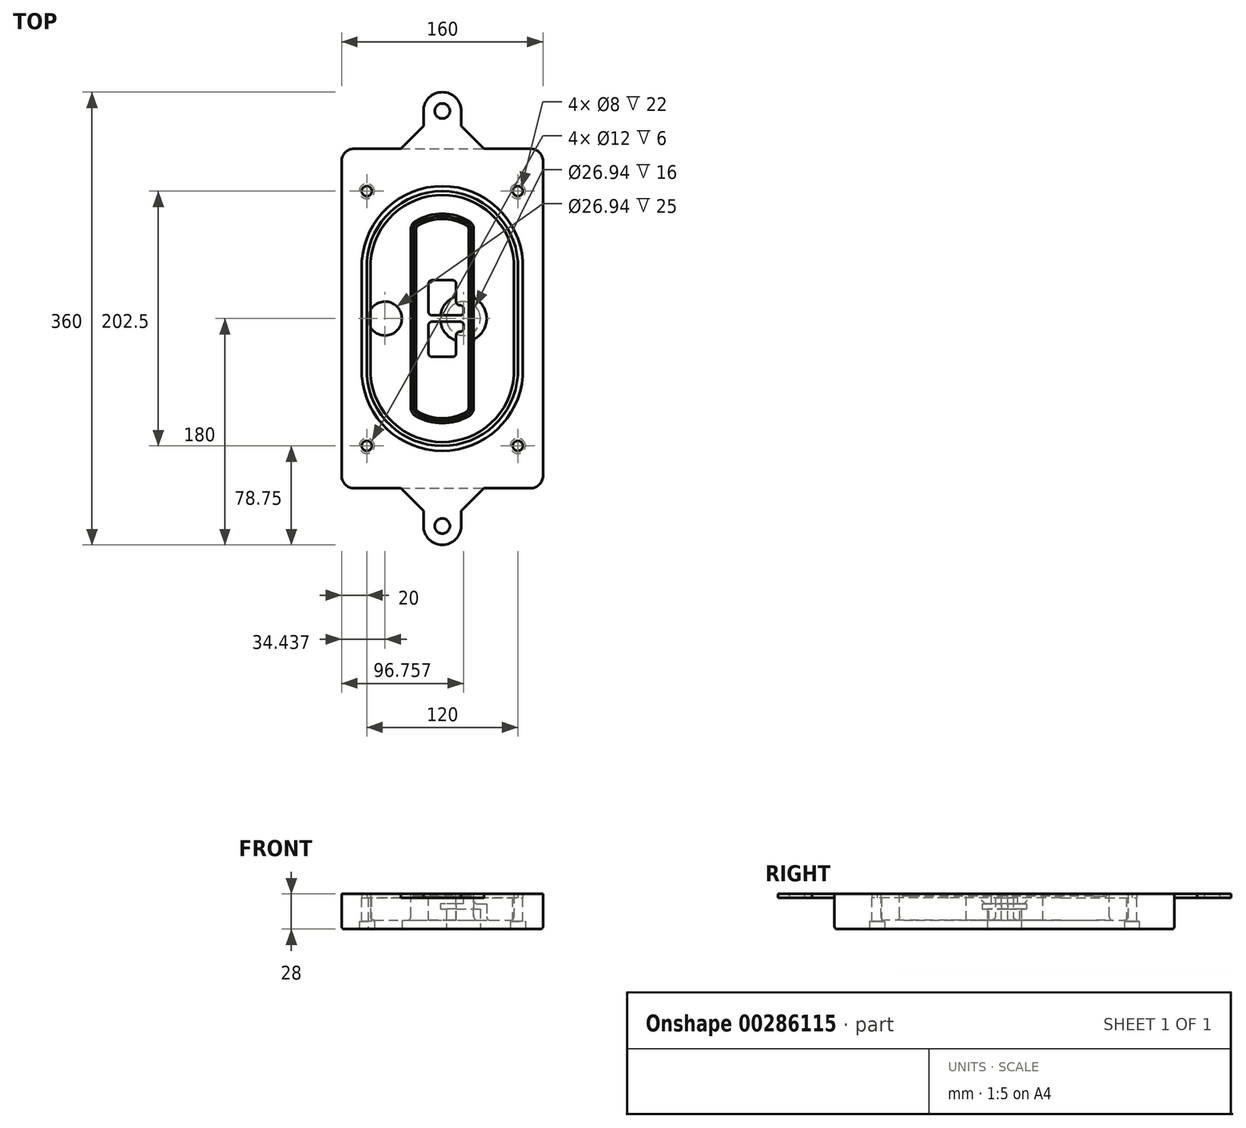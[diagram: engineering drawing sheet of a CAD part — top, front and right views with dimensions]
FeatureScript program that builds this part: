
annotation { "Feature Type Name" : "Feature", "Feature Type Description" : "" }
export const myFeature = defineFeature(function(context is Context, id is Id, definition is map)
    precondition{}
    {
        {
            var Q0;
            Q0=qCreatedBy(makeId("Top.planeOp"),FACE);
            var sketch = newSketch(context, id + "F0", { "sketchPlane" : qUnion([Q0])});
            skPoint(sketch, "E0.rect.middle", {"position": v(0, 0) * mm});
            skLineSegment(sketch, "E1.bottom", {"start": v(-70, -135) * mm, "end": v(70, -135) * mm});
            skLineSegment(sketch, "E1.top", {"start": v(-70, 135) * mm, "end": v(70, 135) * mm});
            skLineSegment(sketch, "E1.left", {"start": v(-80, -125) * mm, "end": v(-80, 125) * mm});
            skLineSegment(sketch, "E1.right", {"start": v(80, -125) * mm, "end": v(80, 125) * mm});
            skLineSegment(sketch, "E2", {"start": v(-80, 135) * mm, "end": v(80, -135) * mm, "construction": true});
            skLineSegment(sketch, "E3", {"start": v(80, 135) * mm, "end": v(-80, -135) * mm, "construction": true});
            skCircle(sketch, "E4", {"center": v(-60, 101.25) * mm, "radius": 4 * mm});
            skCircle(sketch, "E5", {"center": v(60, 101.25) * mm, "radius": 4 * mm});
            skCircle(sketch, "E6", {"center": v(60, -101.25) * mm, "radius": 4 * mm});
            skCircle(sketch, "E7", {"center": v(-60, -101.25) * mm, "radius": 4 * mm});
            skLineSegment(sketch, "E8", {"start": v(-60, 101.25) * mm, "end": v(60, 101.25) * mm, "construction": true});
            skLineSegment(sketch, "E9", {"start": v(60, 101.25) * mm, "end": v(60, -101.25) * mm, "construction": true});
            skLineSegment(sketch, "E10", {"start": v(60, -101.25) * mm, "end": v(-60, -101.25) * mm, "construction": true});
            skLineSegment(sketch, "E11", {"start": v(-60, -101.25) * mm, "end": v(-60, 101.25) * mm, "construction": true});
            skLineSegment(sketch, "E12", {"start": v(-60, 44.66) * mm, "end": v(-60, -44.66) * mm});
            skLineSegment(sketch, "E13", {"start": v(60, 44.66) * mm, "end": v(60, -44.66) * mm});
            skArc(sketch, "E14", {"start": v(59.98, 45.37) * mm, "mid": v(0, 101.25) * mm, "end": v(-59.98, 45.37) * mm});
            skArc(sketch, "E15", {"start": v(-59.98, -45.37) * mm, "mid": v(0, -101.25) * mm, "end": v(59.98, -45.37) * mm});
            skLineSegment(sketch, "E16", {"start": v(-60, 0) * mm, "end": v(60, 0) * mm, "construction": true});
            skPoint(sketch, "E17.visualSharp", {"position": v(-60, -45) * mm});
            skArc(sketch, "E17.filletArc", {"start": v(-60, -44.66) * mm, "mid": v(-60, -45.02) * mm, "end": v(-59.98, -45.37) * mm});
            skPoint(sketch, "E18.visualSharp", {"position": v(-60, 45) * mm});
            skArc(sketch, "E18.filletArc", {"start": v(-59.98, 45.37) * mm, "mid": v(-60, 45.02) * mm, "end": v(-60, 44.66) * mm});
            skPoint(sketch, "E19.visualSharp", {"position": v(60, 45) * mm});
            skArc(sketch, "E19.filletArc", {"start": v(60, 44.66) * mm, "mid": v(60, 45.02) * mm, "end": v(59.98, 45.37) * mm});
            skPoint(sketch, "E20.visualSharp", {"position": v(60, -45) * mm});
            skArc(sketch, "E20.filletArc", {"start": v(59.98, -45.37) * mm, "mid": v(60, -45.02) * mm, "end": v(60, -44.66) * mm});
            skPoint(sketch, "E21.visualSharp", {"position": v(-80, 135) * mm});
            skArc(sketch, "E21.filletArc", {"start": v(-70, 135) * mm, "mid": v(-77.07, 132.07) * mm, "end": v(-80, 125) * mm});
            skPoint(sketch, "E22.visualSharp", {"position": v(80, 135) * mm});
            skArc(sketch, "E22.filletArc", {"start": v(80, 125) * mm, "mid": v(77.07, 132.07) * mm, "end": v(70, 135) * mm});
            skPoint(sketch, "E23.visualSharp", {"position": v(80, -135) * mm});
            skArc(sketch, "E23.filletArc", {"start": v(70, -135) * mm, "mid": v(77.07, -132.07) * mm, "end": v(80, -125) * mm});
            skPoint(sketch, "E24.visualSharp", {"position": v(-80, -135) * mm});
            skArc(sketch, "E24.filletArc", {"start": v(-80, -125) * mm, "mid": v(-77.07, -132.07) * mm, "end": v(-70, -135) * mm});
            skArc(sketch, "E25.0", {"start": v(57, 44.66) * mm, "mid": v(57, 44.9) * mm, "end": v(56.98, 45.16) * mm});
            skLineSegment(sketch, "E25.1", {"start": v(57, 44.66) * mm, "end": v(57, -44.66) * mm});
            skArc(sketch, "E25.2", {"start": v(56.98, -45.16) * mm, "mid": v(57, -44.9) * mm, "end": v(57, -44.66) * mm});
            skArc(sketch, "E25.3", {"start": v(-56.98, -45.16) * mm, "mid": v(0, -98.25) * mm, "end": v(56.98, -45.16) * mm});
            skArc(sketch, "E25.4", {"start": v(-57, -44.66) * mm, "mid": v(-57, -44.9) * mm, "end": v(-56.98, -45.16) * mm});
            skArc(sketch, "E25.5", {"start": v(56.98, 45.16) * mm, "mid": v(0, 98.25) * mm, "end": v(-56.98, 45.16) * mm});
            skLineSegment(sketch, "E25.6", {"start": v(-57, 44.66) * mm, "end": v(-57, -44.66) * mm});
            skArc(sketch, "E25.7", {"start": v(-56.98, 45.16) * mm, "mid": v(-57, 44.9) * mm, "end": v(-57, 44.66) * mm});
            skArc(sketch, "E26.0", {"start": v(-63.97, 45.65) * mm, "mid": v(-64, 45.16) * mm, "end": v(-64, 44.66) * mm});
            skArc(sketch, "E26.1", {"start": v(63.97, 45.65) * mm, "mid": v(0, 105.25) * mm, "end": v(-63.97, 45.65) * mm});
            skArc(sketch, "E26.2", {"start": v(64, 44.66) * mm, "mid": v(64, 45.16) * mm, "end": v(63.97, 45.65) * mm});
            skLineSegment(sketch, "E26.3", {"start": v(64, 44.66) * mm, "end": v(64, -44.66) * mm});
            skArc(sketch, "E26.4", {"start": v(63.97, -45.65) * mm, "mid": v(64, -45.16) * mm, "end": v(64, -44.66) * mm});
            skLineSegment(sketch, "E26.5", {"start": v(-64, 44.66) * mm, "end": v(-64, -44.66) * mm});
            skArc(sketch, "E26.6", {"start": v(-63.97, -45.65) * mm, "mid": v(0, -105.25) * mm, "end": v(63.97, -45.65) * mm});
            skArc(sketch, "E26.7", {"start": v(-64, -44.66) * mm, "mid": v(-64, -45.16) * mm, "end": v(-63.97, -45.65) * mm});
            skSolve(sketch);
        }
        {
            var Q0;
            Q0=makeQuery(id+"F0.imprint","IMPRINT",FACE,{"disambiguationData":[TD([[makeQuery(id+"F0.imprint","IMPRINT",EDGE,{"derivedFrom":sQuery(id+"F0.wireOp",EDGE,"E1.bottom")}),1.0]])]});
            var Q1;
            Q1=makeQuery(id+"F0.imprint","IMPRINT",FACE,{"disambiguationData":[TD([[makeQuery(id+"F0.imprint","IMPRINT",EDGE,{"derivedFrom":sQuery(id+"F0.wireOp",EDGE,"E12")}),1.0]])]});
            var Q2;
            Q2=makeQuery(id+"F0.imprint","IMPRINT",FACE,{"disambiguationData":[TD([[makeQuery(id+"F0.imprint","IMPRINT",EDGE,{"derivedFrom":sQuery(id+"F0.wireOp",EDGE,"E25.0")}),1.0]])]});
            var Q3;
            Q3=makeQuery(id+"F0.imprint","IMPRINT",FACE,{"disambiguationData":[TD([[makeQuery(id+"F0.imprint","IMPRINT",EDGE,{"derivedFrom":sQuery(id+"F0.wireOp",EDGE,"E12")}),-1.0]])]});
            extrude(context, id + "F1", {"entities" : qUnion([Q0, Q1, Q2, Q3]), "oppositeDirection" : true, "depth" : 25 * mm});
        }
        {
            var Q0;
            Q0=makeQuery(id+"F0.imprint","IMPRINT",FACE,{"disambiguationData":[TD([[makeQuery(id+"F0.imprint","IMPRINT",EDGE,{"derivedFrom":sQuery(id+"F0.wireOp",EDGE,"E12")}),1.0]])]});
            extrude(context, id + "F2", {"entities" : qUnion([Q0]), "operationType" : NewBodyOperationType.ADD, "depth" : 3 * mm});
        }
        {
            var Q0;
            Q0=makeQuery(id+"F0.imprint","IMPRINT",FACE,{"disambiguationData":[TD([[makeQuery(id+"F0.imprint","IMPRINT",EDGE,{"derivedFrom":sQuery(id+"F0.wireOp",EDGE,"E25.0")}),1.0]])]});
            extrude(context, id + "F3", {"entities" : qUnion([Q0]), "operationType" : NewBodyOperationType.REMOVE, "oppositeDirection" : true, "depth" : 18 * mm});
        }
        {
            var Q0;
            Q0=makeQuery(id+"F2.opExtrude","CAP_FACE",FACE,{"disambiguationData":[OSD([sQuery(id+"F0.wireOp",EDGE,"E12"),sQuery(id+"F0.wireOp",EDGE,"E13"),sQuery(id+"F0.wireOp",EDGE,"E14"),sQuery(id+"F0.wireOp",EDGE,"E15"),sQuery(id+"F0.wireOp",EDGE,"E17.filletArc"),sQuery(id+"F0.wireOp",EDGE,"E18.filletArc"),sQuery(id+"F0.wireOp",EDGE,"E19.filletArc"),sQuery(id+"F0.wireOp",EDGE,"E20.filletArc"),sQuery(id+"F0.wireOp",EDGE,"E25.0"),sQuery(id+"F0.wireOp",EDGE,"E25.1"),sQuery(id+"F0.wireOp",EDGE,"E25.2"),sQuery(id+"F0.wireOp",EDGE,"E25.3"),sQuery(id+"F0.wireOp",EDGE,"E25.4"),sQuery(id+"F0.wireOp",EDGE,"E25.5"),sQuery(id+"F0.wireOp",EDGE,"E25.6"),sQuery(id+"F0.wireOp",EDGE,"E25.7")])],"isStart":false});
            var sketch = newSketch(context, id + "F4", { "sketchPlane" : qUnion([Q0])});
            skArc(sketch, "E27.0", {"start": v(-20.99, -77.65) * mm, "mid": v(0, -83.25) * mm, "end": v(20.99, -77.65) * mm});
            skArc(sketch, "E28.0", {"start": v(20.99, 77.65) * mm, "mid": v(0, 83.25) * mm, "end": v(-20.99, 77.65) * mm});
            skLineSegment(sketch, "E29", {"start": v(-25, 70.71) * mm, "end": v(-25, -70.71) * mm});
            skLineSegment(sketch, "E30", {"start": v(25, 70.71) * mm, "end": v(25, -70.71) * mm});
            skLineSegment(sketch, "E31", {"start": v(-25, 75.03) * mm, "end": v(25, 75.03) * mm, "construction": true});
            skLineSegment(sketch, "E32", {"start": v(-25, -75.03) * mm, "end": v(25, -75.03) * mm, "construction": true});
            skPoint(sketch, "E33.visualSharp", {"position": v(-25, 75.03) * mm});
            skArc(sketch, "E33.filletArc", {"start": v(-20.99, 77.65) * mm, "mid": v(-23.92, 74.72) * mm, "end": v(-25, 70.71) * mm});
            skPoint(sketch, "E34.visualSharp", {"position": v(25, 75.03) * mm});
            skArc(sketch, "E34.filletArc", {"start": v(25, 70.71) * mm, "mid": v(23.92, 74.72) * mm, "end": v(20.99, 77.65) * mm});
            skPoint(sketch, "E35.visualSharp", {"position": v(25, -75.03) * mm});
            skArc(sketch, "E35.filletArc", {"start": v(20.99, -77.65) * mm, "mid": v(23.92, -74.72) * mm, "end": v(25, -70.71) * mm});
            skPoint(sketch, "E36.visualSharp", {"position": v(-25, -75.03) * mm});
            skArc(sketch, "E36.filletArc", {"start": v(-25, -70.71) * mm, "mid": v(-23.92, -74.72) * mm, "end": v(-20.99, -77.65) * mm});
            skArc(sketch, "E37.0", {"start": v(56.98, 45.16) * mm, "mid": v(0, 98.25) * mm, "end": v(-56.98, 45.16) * mm});
            skArc(sketch, "E37.1", {"start": v(-56.98, 45.16) * mm, "mid": v(-57, 44.9) * mm, "end": v(-57, 44.66) * mm});
            skLineSegment(sketch, "E37.2", {"start": v(-57, 44.66) * mm, "end": v(-57, -44.66) * mm});
            skArc(sketch, "E37.3", {"start": v(-57, -44.66) * mm, "mid": v(-57, -44.9) * mm, "end": v(-56.98, -45.16) * mm});
            skArc(sketch, "E37.4", {"start": v(-56.98, -45.16) * mm, "mid": v(0, -98.25) * mm, "end": v(56.98, -45.16) * mm});
            skArc(sketch, "E37.5", {"start": v(56.98, -45.16) * mm, "mid": v(57, -44.9) * mm, "end": v(57, -44.66) * mm});
            skLineSegment(sketch, "E37.6", {"start": v(57, 44.66) * mm, "end": v(57, -44.66) * mm});
            skArc(sketch, "E37.7", {"start": v(57, 44.66) * mm, "mid": v(57, 44.9) * mm, "end": v(56.98, 45.16) * mm});
            skLineSegment(sketch, "E38.0", {"start": v(23, 70.71) * mm, "end": v(23, -70.71) * mm});
            skArc(sketch, "E38.1", {"start": v(19.99, -75.92) * mm, "mid": v(22.2, -73.72) * mm, "end": v(23, -70.71) * mm});
            skArc(sketch, "E38.2", {"start": v(-19.99, -75.92) * mm, "mid": v(0, -81.25) * mm, "end": v(19.99, -75.92) * mm});
            skArc(sketch, "E38.3", {"start": v(-23, -70.71) * mm, "mid": v(-22.2, -73.72) * mm, "end": v(-19.99, -75.92) * mm});
            skLineSegment(sketch, "E38.4", {"start": v(-23, 70.71) * mm, "end": v(-23, -70.71) * mm});
            skArc(sketch, "E38.5", {"start": v(23, 70.71) * mm, "mid": v(22.2, 73.72) * mm, "end": v(19.99, 75.92) * mm});
            skArc(sketch, "E38.6", {"start": v(-19.99, 75.92) * mm, "mid": v(-22.2, 73.72) * mm, "end": v(-23, 70.71) * mm});
            skArc(sketch, "E38.7", {"start": v(19.99, 75.92) * mm, "mid": v(0, 81.25) * mm, "end": v(-19.99, 75.92) * mm});
            skArc(sketch, "E39.0", {"start": v(21, 70.71) * mm, "mid": v(20.46, 72.72) * mm, "end": v(19, 74.18) * mm});
            skLineSegment(sketch, "E39.1", {"start": v(21, 70.71) * mm, "end": v(21, -70.71) * mm});
            skArc(sketch, "E39.2", {"start": v(19, -74.18) * mm, "mid": v(20.46, -72.72) * mm, "end": v(21, -70.71) * mm});
            skArc(sketch, "E39.3", {"start": v(-19, -74.18) * mm, "mid": v(0, -79.25) * mm, "end": v(19, -74.18) * mm});
            skArc(sketch, "E39.4", {"start": v(-21, -70.71) * mm, "mid": v(-20.46, -72.72) * mm, "end": v(-19, -74.18) * mm});
            skArc(sketch, "E39.5", {"start": v(19, 74.18) * mm, "mid": v(0, 79.25) * mm, "end": v(-19, 74.18) * mm});
            skLineSegment(sketch, "E39.6", {"start": v(-21, 70.71) * mm, "end": v(-21, -70.71) * mm});
            skArc(sketch, "E39.7", {"start": v(-19, 74.18) * mm, "mid": v(-20.46, 72.72) * mm, "end": v(-21, 70.71) * mm});
            skLineSegment(sketch, "E40", {"start": v(-25, 0) * mm, "end": v(25, 0) * mm, "construction": true});
            skLineSegment(sketch, "E41", {"start": v(-11, 5.5) * mm, "end": v(-11, 27.5) * mm});
            skLineSegment(sketch, "E42", {"start": v(-8, 30.5) * mm, "end": v(8, 30.5) * mm});
            skLineSegment(sketch, "E43", {"start": v(11, 27.5) * mm, "end": v(11, 13.5) * mm});
            skLineSegment(sketch, "E44", {"start": v(14, 10.5) * mm, "end": v(14, 10.5) * mm});
            skLineSegment(sketch, "E45", {"start": v(17, 7.5) * mm, "end": v(17, 5.5) * mm});
            skLineSegment(sketch, "E46", {"start": v(14, 2.5) * mm, "end": v(-8, 2.5) * mm});
            skPoint(sketch, "E47.visualSharp", {"position": v(-11, 30.5) * mm});
            skArc(sketch, "E47.filletArc", {"start": v(-8, 30.5) * mm, "mid": v(-10.12, 29.62) * mm, "end": v(-11, 27.5) * mm});
            skPoint(sketch, "E48.visualSharp", {"position": v(11, 30.5) * mm});
            skArc(sketch, "E48.filletArc", {"start": v(11, 27.5) * mm, "mid": v(10.12, 29.62) * mm, "end": v(8, 30.5) * mm});
            skPoint(sketch, "E49.visualSharp", {"position": v(11, 10.5) * mm});
            skArc(sketch, "E49.filletArc", {"start": v(11, 13.5) * mm, "mid": v(11.88, 11.38) * mm, "end": v(14, 10.5) * mm});
            skPoint(sketch, "E50.visualSharp", {"position": v(17, 10.5) * mm});
            skArc(sketch, "E50.filletArc", {"start": v(17, 7.5) * mm, "mid": v(16.12, 9.62) * mm, "end": v(14, 10.5) * mm});
            skPoint(sketch, "E51.visualSharp", {"position": v(17, 2.5) * mm});
            skArc(sketch, "E51.filletArc", {"start": v(14, 2.5) * mm, "mid": v(16.12, 3.38) * mm, "end": v(17, 5.5) * mm});
            skPoint(sketch, "E52.visualSharp", {"position": v(-11, 2.5) * mm});
            skArc(sketch, "E52.filletArc", {"start": v(-11, 5.5) * mm, "mid": v(-10.12, 3.38) * mm, "end": v(-8, 2.5) * mm});
            skLineSegment(sketch, "E53.0.MirrorCS", {"start": v(14, -2.5) * mm, "end": v(-8, -2.5) * mm});
            skArc(sketch, "E54.0.MirrorCS", {"start": v(-11, -5.5) * mm, "mid": v(-10.12, -3.38) * mm, "end": v(-8, -2.5) * mm});
            skLineSegment(sketch, "E55.0.MirrorCS", {"start": v(-11, -5.5) * mm, "end": v(-11, -27.5) * mm});
            skArc(sketch, "E56.0.MirrorCS", {"start": v(-8, -30.5) * mm, "mid": v(-10.12, -29.62) * mm, "end": v(-11, -27.5) * mm});
            skLineSegment(sketch, "E57.0.MirrorCS", {"start": v(-8, -30.5) * mm, "end": v(8, -30.5) * mm});
            skArc(sketch, "E58.0.MirrorCS", {"start": v(11, -27.5) * mm, "mid": v(10.12, -29.62) * mm, "end": v(8, -30.5) * mm});
            skLineSegment(sketch, "E59.0.MirrorCS", {"start": v(11, -27.5) * mm, "end": v(11, -13.5) * mm});
            skArc(sketch, "E60.0.MirrorCS", {"start": v(11, -13.5) * mm, "mid": v(11.88, -11.38) * mm, "end": v(14, -10.5) * mm});
            skArc(sketch, "E61.0.MirrorCS", {"start": v(17, -7.5) * mm, "mid": v(16.12, -9.62) * mm, "end": v(14, -10.5) * mm});
            skLineSegment(sketch, "E62.0.MirrorCS", {"start": v(17, -7.5) * mm, "end": v(17, -5.5) * mm});
            skArc(sketch, "E63.0.MirrorCS", {"start": v(14, -2.5) * mm, "mid": v(16.12, -3.38) * mm, "end": v(17, -5.5) * mm});
            skSolve(sketch);
        }
        {
            var Q0;
            Q0=makeQuery(id+"F4.imprint","IMPRINT",FACE,{"disambiguationData":[TD([[makeQuery(id+"F4.imprint","IMPRINT",EDGE,{"derivedFrom":sQuery(id+"F4.wireOp",EDGE,"E27.0")}),1.0]])]});
            var Q1;
            Q1=makeQuery(id+"F4.imprint","IMPRINT",FACE,{"disambiguationData":[TD([[makeQuery(id+"F4.imprint","IMPRINT",EDGE,{"derivedFrom":sQuery(id+"F4.wireOp",EDGE,"E38.0")}),-1.0]])]});
            var Q2;
            Q2=makeQuery(id+"F4.imprint","IMPRINT",FACE,{"disambiguationData":[TD([[makeQuery(id+"F4.imprint","IMPRINT",EDGE,{"derivedFrom":sQuery(id+"F4.wireOp",EDGE,"E39.0")}),1.0]])]});
            extrude(context, id + "F5", {"entities" : qUnion([Q0, Q1, Q2]), "operationType" : NewBodyOperationType.ADD, "endBound" : BoundingType.UP_TO_NEXT, "oppositeDirection" : true, "depth" : 25 * mm});
        }
        {
            var Q0;
            Q0=makeQuery(id+"F4.imprint","IMPRINT",FACE,{"disambiguationData":[TD([[makeQuery(id+"F4.imprint","IMPRINT",EDGE,{"derivedFrom":sQuery(id+"F4.wireOp",EDGE,"E38.0")}),-1.0]])]});
            extrude(context, id + "F6", {"entities" : qUnion([Q0]), "operationType" : NewBodyOperationType.REMOVE, "oppositeDirection" : true, "depth" : 2 * mm});
        }
        {
            var Q0;
            Q0=makeQuery(id+"F1.opExtrude","CAP_FACE",FACE,{"disambiguationData":[OSD([sQuery(id+"F0.wireOp",EDGE,"E1.bottom"),sQuery(id+"F0.wireOp",EDGE,"E1.top"),sQuery(id+"F0.wireOp",EDGE,"E1.left"),sQuery(id+"F0.wireOp",EDGE,"E1.right"),sQuery(id+"F0.wireOp",EDGE,"E4"),sQuery(id+"F0.wireOp",EDGE,"E5"),sQuery(id+"F0.wireOp",EDGE,"E6"),sQuery(id+"F0.wireOp",EDGE,"E7"),sQuery(id+"F0.wireOp",EDGE,"E21.filletArc"),sQuery(id+"F0.wireOp",EDGE,"E22.filletArc"),sQuery(id+"F0.wireOp",EDGE,"E23.filletArc"),sQuery(id+"F0.wireOp",EDGE,"E24.filletArc")])],"isStart":false});
            var sketch = newSketch(context, id + "F7", { "sketchPlane" : qUnion([Q0])});
            skCircle(sketch, "E64", {"center": v(16.76, 0) * mm, "radius": 13.47 * mm});
            skCircle(sketch, "E65", {"center": v(-45.56, 0) * mm, "radius": 13.47 * mm});
            skLineSegment(sketch, "E66", {"start": v(80, 0) * mm, "end": v(-80, 0) * mm});
            skCircle(sketch, "E67", {"center": v(16.76, 0) * mm, "radius": 18.47 * mm});
            skCircle(sketch, "E68", {"center": v(60, -101.25) * mm, "radius": 6 * mm});
            skCircle(sketch, "E69", {"center": v(-60, -101.25) * mm, "radius": 6 * mm});
            skCircle(sketch, "E70", {"center": v(-60, 101.25) * mm, "radius": 6 * mm});
            skCircle(sketch, "E71", {"center": v(60, 101.25) * mm, "radius": 6 * mm});
            skSolve(sketch);
        }
        {
            var Q0;
            {var subQ1=sQuery(id+"F7.wireOp",EDGE,"E66");var subQ4=sQuery(id+"F7.wireOp",EDGE,"E64");var subQ6=makeQuery(id+"F7.imprint","INTERSECT",VERTEX,{"disambiguationData":[OD(0.0)],"derivedFrom":[subQ4,subQ1]});Q0=makeQuery(id+"F7.imprint","IMPRINT",FACE,{"disambiguationData":[TD([[makeQuery(id+"F7.imprint","IMPRINT",EDGE,{"disambiguationData":[TD([[subQ6,-1.0]])],"derivedFrom":subQ4}),-1.0]])]});}
            var Q1;
            {var subQ0=sQuery(id+"F7.wireOp",EDGE,"E66");var subQ1=sQuery(id+"F7.wireOp",EDGE,"E64");var subQ3=makeQuery(id+"F7.imprint","INTERSECT",VERTEX,{"disambiguationData":[OD(0.0)],"derivedFrom":[subQ1,subQ0]});Q1=makeQuery(id+"F7.imprint","IMPRINT",FACE,{"disambiguationData":[TD([[makeQuery(id+"F7.imprint","IMPRINT",EDGE,{"disambiguationData":[TD([[subQ3,-1.0]])],"derivedFrom":subQ1}),1.0]])]});}
            var Q2;
            {var subQ0=sQuery(id+"F7.wireOp",EDGE,"E66");var subQ1=sQuery(id+"F7.wireOp",EDGE,"E64");var subQ3=makeQuery(id+"F7.imprint","INTERSECT",VERTEX,{"disambiguationData":[OD(0.0)],"derivedFrom":[subQ1,subQ0]});Q2=makeQuery(id+"F7.imprint","IMPRINT",FACE,{"disambiguationData":[TD([[makeQuery(id+"F7.imprint","IMPRINT",EDGE,{"disambiguationData":[TD([[subQ3,1.0]])],"derivedFrom":subQ1}),1.0]])]});}
            var Q3;
            {var subQ1=sQuery(id+"F7.wireOp",EDGE,"E66");var subQ4=sQuery(id+"F7.wireOp",EDGE,"E64");var subQ6=makeQuery(id+"F7.imprint","INTERSECT",VERTEX,{"disambiguationData":[OD(0.0)],"derivedFrom":[subQ4,subQ1]});Q3=makeQuery(id+"F7.imprint","IMPRINT",FACE,{"disambiguationData":[TD([[makeQuery(id+"F7.imprint","IMPRINT",EDGE,{"disambiguationData":[TD([[subQ6,1.0]])],"derivedFrom":subQ4}),-1.0]])]});}
            extrude(context, id + "F8", {"entities" : qUnion([Q0, Q1, Q2, Q3]), "operationType" : NewBodyOperationType.ADD, "oppositeDirection" : true, "depth" : 20 * mm});
        }
        {
            var Q0;
            {var subQ0=sQuery(id+"F7.wireOp",EDGE,"E66");var subQ1=sQuery(id+"F7.wireOp",EDGE,"E64");var subQ3=makeQuery(id+"F7.imprint","INTERSECT",VERTEX,{"disambiguationData":[OD(0.0)],"derivedFrom":[subQ1,subQ0]});Q0=makeQuery(id+"F7.imprint","IMPRINT",FACE,{"disambiguationData":[TD([[makeQuery(id+"F7.imprint","IMPRINT",EDGE,{"disambiguationData":[TD([[subQ3,-1.0]])],"derivedFrom":subQ1}),1.0]])]});}
            var Q1;
            {var subQ0=sQuery(id+"F7.wireOp",EDGE,"E66");var subQ1=sQuery(id+"F7.wireOp",EDGE,"E64");var subQ3=makeQuery(id+"F7.imprint","INTERSECT",VERTEX,{"disambiguationData":[OD(0.0)],"derivedFrom":[subQ1,subQ0]});Q1=makeQuery(id+"F7.imprint","IMPRINT",FACE,{"disambiguationData":[TD([[makeQuery(id+"F7.imprint","IMPRINT",EDGE,{"disambiguationData":[TD([[subQ3,1.0]])],"derivedFrom":subQ1}),1.0]])]});}
            extrude(context, id + "F9", {"entities" : qUnion([Q0, Q1]), "operationType" : NewBodyOperationType.REMOVE, "oppositeDirection" : true, "depth" : 16 * mm});
        }
        {
            var Q0;
            {var subQ0=sQuery(id+"F7.wireOp",EDGE,"E66");var subQ1=sQuery(id+"F7.wireOp",EDGE,"E65");var subQ3=makeQuery(id+"F7.imprint","INTERSECT",VERTEX,{"disambiguationData":[OD(0.0)],"derivedFrom":[subQ1,subQ0]});Q0=makeQuery(id+"F7.imprint","IMPRINT",FACE,{"disambiguationData":[TD([[makeQuery(id+"F7.imprint","IMPRINT",EDGE,{"disambiguationData":[TD([[subQ3,-1.0]])],"derivedFrom":subQ1}),1.0]])]});}
            var Q1;
            {var subQ0=sQuery(id+"F7.wireOp",EDGE,"E66");var subQ1=sQuery(id+"F7.wireOp",EDGE,"E65");var subQ3=makeQuery(id+"F7.imprint","INTERSECT",VERTEX,{"disambiguationData":[OD(0.0)],"derivedFrom":[subQ1,subQ0]});Q1=makeQuery(id+"F7.imprint","IMPRINT",FACE,{"disambiguationData":[TD([[makeQuery(id+"F7.imprint","IMPRINT",EDGE,{"disambiguationData":[TD([[subQ3,1.0]])],"derivedFrom":subQ1}),1.0]])]});}
            extrude(context, id + "F10", {"entities" : qUnion([Q0, Q1]), "operationType" : NewBodyOperationType.REMOVE, "oppositeDirection" : true, "depth" : 25 * mm});
        }
        {
            var Q0;
            Q0=makeQuery(id+"F7.imprint","IMPRINT",FACE,{"disambiguationData":[TD([[makeQuery(id+"F7.imprint","IMPRINT",EDGE,{"derivedFrom":sQuery(id+"F7.wireOp",EDGE,"E68")}),1.0]])]});
            var Q1;
            Q1=makeQuery(id+"F7.imprint","IMPRINT",FACE,{"disambiguationData":[TD([[makeQuery(id+"F7.imprint","IMPRINT",EDGE,{"derivedFrom":makeQuery(id+"F1.opExtrude","CAP_EDGE",EDGE,{"disambiguationData":[OSD([sQuery(id+"F0.wireOp",EDGE,"E5")])],"isStart":false})}),-1.0]])]});
            var Q2;
            Q2=makeQuery(id+"F7.imprint","IMPRINT",FACE,{"disambiguationData":[TD([[makeQuery(id+"F7.imprint","IMPRINT",EDGE,{"derivedFrom":sQuery(id+"F7.wireOp",EDGE,"E69")}),1.0]])]});
            var Q3;
            Q3=makeQuery(id+"F7.imprint","IMPRINT",FACE,{"disambiguationData":[TD([[makeQuery(id+"F7.imprint","IMPRINT",EDGE,{"derivedFrom":makeQuery(id+"F1.opExtrude","CAP_EDGE",EDGE,{"disambiguationData":[OSD([sQuery(id+"F0.wireOp",EDGE,"E4")])],"isStart":false})}),-1.0]])]});
            var Q4;
            Q4=makeQuery(id+"F7.imprint","IMPRINT",FACE,{"disambiguationData":[TD([[makeQuery(id+"F7.imprint","IMPRINT",EDGE,{"derivedFrom":sQuery(id+"F7.wireOp",EDGE,"E70")}),1.0]])]});
            var Q5;
            Q5=makeQuery(id+"F7.imprint","IMPRINT",FACE,{"disambiguationData":[TD([[makeQuery(id+"F7.imprint","IMPRINT",EDGE,{"derivedFrom":makeQuery(id+"F1.opExtrude","CAP_EDGE",EDGE,{"disambiguationData":[OSD([sQuery(id+"F0.wireOp",EDGE,"E7")])],"isStart":false})}),-1.0]])]});
            var Q6;
            Q6=makeQuery(id+"F7.imprint","IMPRINT",FACE,{"disambiguationData":[TD([[makeQuery(id+"F7.imprint","IMPRINT",EDGE,{"derivedFrom":sQuery(id+"F7.wireOp",EDGE,"E71")}),1.0]])]});
            var Q7;
            Q7=makeQuery(id+"F7.imprint","IMPRINT",FACE,{"disambiguationData":[TD([[makeQuery(id+"F7.imprint","IMPRINT",EDGE,{"derivedFrom":makeQuery(id+"F1.opExtrude","CAP_EDGE",EDGE,{"disambiguationData":[OSD([sQuery(id+"F0.wireOp",EDGE,"E6")])],"isStart":false})}),-1.0]])]});
            extrude(context, id + "F11", {"entities" : qUnion([Q0, Q1, Q2, Q3, Q4, Q5, Q6, Q7]), "operationType" : NewBodyOperationType.REMOVE, "oppositeDirection" : true, "depth" : 6 * mm});
        }
        {
            var Q0;
            Q0=makeQuery(id+"F9.boolean.opBoolean","COPY",FACE,{"derivedFrom":makeQuery(id+"F9.opExtrude","CAP_FACE",FACE,{"disambiguationData":[OSD([sQuery(id+"F7.wireOp",EDGE,"E64")])],"isStart":false})});
            var sketch = newSketch(context, id + "F12", { "sketchPlane" : qUnion([Q0])});
            skArc(sketch, "E72.0", {"start": v(11, 17.55) * mm, "mid": v(2.57, 11.82) * mm, "end": v(-1.54, 2.5) * mm});
            skArc(sketch, "E72.1", {"start": v(-1.54, -2.5) * mm, "mid": v(2.57, -11.82) * mm, "end": v(11, -17.55) * mm});
            skLineSegment(sketch, "E73", {"start": v(-1.54, -2.5) * mm, "end": v(14, -2.5) * mm});
            skLineSegment(sketch, "E74.0", {"start": v(14, 2.5) * mm, "end": v(-1.54, 2.5) * mm});
            skArc(sketch, "E74.1", {"start": v(14, 2.5) * mm, "mid": v(16.12, 3.38) * mm, "end": v(17, 5.5) * mm});
            skLineSegment(sketch, "E74.2", {"start": v(17, 7.5) * mm, "end": v(17, 5.5) * mm});
            skArc(sketch, "E74.3", {"start": v(17, 7.5) * mm, "mid": v(16.12, 9.62) * mm, "end": v(14, 10.5) * mm});
            skArc(sketch, "E74.4", {"start": v(11, 13.5) * mm, "mid": v(11.88, 11.38) * mm, "end": v(14, 10.5) * mm});
            skLineSegment(sketch, "E74.5", {"start": v(11, 17.55) * mm, "end": v(11, 13.5) * mm});
            skLineSegment(sketch, "E74.7", {"start": v(14, -2.5) * mm, "end": v(-1.54, -2.5) * mm});
            skArc(sketch, "E74.8", {"start": v(14, -2.5) * mm, "mid": v(16.12, -3.38) * mm, "end": v(17, -5.5) * mm});
            skLineSegment(sketch, "E74.9", {"start": v(17, -7.5) * mm, "end": v(17, -5.5) * mm});
            skArc(sketch, "E74.10", {"start": v(17, -7.5) * mm, "mid": v(16.12, -9.62) * mm, "end": v(14, -10.5) * mm});
            skArc(sketch, "E74.11", {"start": v(11, -13.5) * mm, "mid": v(11.88, -11.38) * mm, "end": v(14, -10.5) * mm});
            skLineSegment(sketch, "E74.12", {"start": v(11, -17.55) * mm, "end": v(11, -13.5) * mm});
            skPoint(sketch, "E75.orphan", {"position": v(11, -27.5) * mm});
            skPoint(sketch, "E76.orphan", {"position": v(-8, -2.5) * mm});
            skPoint(sketch, "E77.orphan", {"position": v(-8, 2.5) * mm});
            skPoint(sketch, "E78.orphan", {"position": v(11, 27.5) * mm});
            skSolve(sketch);
        }
        {
            var Q0;
            {var subQ7=sQuery(id+"F12.wireOp",EDGE,"E72.0");var subQ14=sQuery(id+"F12.wireOp",EDGE,"E72.1");var subQ16=sQuery(id+"F12.wireOp",EDGE,"E74.1");var subQ18=sQuery(id+"F12.wireOp",EDGE,"E74.8");Q0=qUnion([makeQuery(id+"F12.imprint","IMPRINT",FACE,{"disambiguationData":[TD([[makeQuery(id+"F12.imprint","IMPRINT",EDGE,{"derivedFrom":subQ7}),1.0]])]}),makeQuery(id+"F12.imprint","IMPRINT",FACE,{"disambiguationData":[TD([[makeQuery(id+"F12.imprint","IMPRINT",EDGE,{"derivedFrom":subQ14}),1.0]])]}),makeQuery(id+"F12.imprint","IMPRINT",FACE,{"disambiguationData":[TD([[makeQuery(id+"F12.imprint","IMPRINT",EDGE,{"derivedFrom":subQ16}),1.0]])]}),makeQuery(id+"F12.imprint","IMPRINT",FACE,{"disambiguationData":[TD([[makeQuery(id+"F12.imprint","IMPRINT",EDGE,{"derivedFrom":subQ18}),-1.0]])]})]);}
            var Q1;
            Q1=makeQuery(id+"F5.boolean.opBoolean","SPLIT",FACE,{"disambiguationData":[TD([makeQuery(id+"F5.opExtrude","SWEPT_FACE",FACE,{"disambiguationData":[OSD([sQuery(id+"F4.wireOp",EDGE,"E41")])]})])],"derivedFrom":makeQuery(id+"F3.boolean.opBoolean","COPY",FACE,{"derivedFrom":makeQuery(id+"F3.opExtrude","CAP_FACE",FACE,{"disambiguationData":[OSD([sQuery(id+"F0.wireOp",EDGE,"E25.0"),sQuery(id+"F0.wireOp",EDGE,"E25.1"),sQuery(id+"F0.wireOp",EDGE,"E25.2"),sQuery(id+"F0.wireOp",EDGE,"E25.3"),sQuery(id+"F0.wireOp",EDGE,"E25.4"),sQuery(id+"F0.wireOp",EDGE,"E25.5"),sQuery(id+"F0.wireOp",EDGE,"E25.6"),sQuery(id+"F0.wireOp",EDGE,"E25.7")])],"isStart":false})})});
            extrude(context, id + "F13", {"entities" : qUnion([Q0]), "operationType" : NewBodyOperationType.REMOVE, "endBound" : BoundingType.UP_TO_SURFACE, "endBoundEntityFace" : qUnion([Q1]), "depth" : 25 * mm});
        }
        {
            var Q0;
            Q0=makeQuery(id+"F3.boolean.opBoolean","COPY",EDGE,{"derivedFrom":makeQuery(id+"F3.opExtrude","CAP_EDGE",EDGE,{"disambiguationData":[OSD([sQuery(id+"F0.wireOp",EDGE,"E25.6")])],"isStart":false})});
            var Q1;
            Q1=makeQuery(id+"F8.boolean.opBoolean","INTERSECT",EDGE,{"derivedFrom":[makeQuery(id+"F5.opExtrude","SWEPT_FACE",FACE,{"disambiguationData":[OSD([sQuery(id+"F4.wireOp",EDGE,"E30")])]}),makeQuery(id+"F8.opExtrude","CAP_FACE",FACE,{"disambiguationData":[OSD([sQuery(id+"F7.wireOp",EDGE,"E67")])],"isStart":false})]});
            var Q2;
            Q2=makeQuery(id+"F8.boolean.opBoolean","INTERSECT",EDGE,{"disambiguationData":[OD(1.0)],"derivedFrom":[makeQuery(id+"F5.opExtrude","SWEPT_FACE",FACE,{"disambiguationData":[OSD([sQuery(id+"F4.wireOp",EDGE,"E30")])]}),makeQuery(id+"F8.opExtrude","SWEPT_FACE",FACE,{"disambiguationData":[OSD([sQuery(id+"F7.wireOp",EDGE,"E67")])]})]});
            var Q3;
            {var subQ0=sQuery(id+"F4.wireOp",EDGE,"E30");Q3=makeQuery(id+"F8.boolean.opBoolean","SPLIT",EDGE,{"disambiguationData":[TD([makeQuery(id+"F5.opExtrude","SWEPT_FACE",FACE,{"disambiguationData":[OSD([sQuery(id+"F4.wireOp",EDGE,"E35.filletArc")])]})])],"derivedFrom":makeQuery(id+"F5.opExtrude","CAP_EDGE",EDGE,{"disambiguationData":[OSD([subQ0])],"isStart":false})});}
            var Q4;
            {var subQ0=sQuery(id+"F0.wireOp",EDGE,"E25.7");var subQ1=sQuery(id+"F0.wireOp",EDGE,"E25.1");var subQ2=sQuery(id+"F0.wireOp",EDGE,"E25.6");var subQ3=sQuery(id+"F0.wireOp",EDGE,"E25.5");var subQ4=sQuery(id+"F0.wireOp",EDGE,"E25.4");var subQ5=sQuery(id+"F0.wireOp",EDGE,"E25.0");var subQ6=sQuery(id+"F0.wireOp",EDGE,"E25.2");var subQ7=sQuery(id+"F0.wireOp",EDGE,"E25.3");Q4=makeQuery(id+"F8.boolean.opBoolean","INTERSECT",EDGE,{"derivedFrom":[makeQuery(id+"F5.boolean.opBoolean","SPLIT",FACE,{"disambiguationData":[TD([makeQuery(id+"F2.opExtrude","SWEPT_FACE",FACE,{"disambiguationData":[OSD([subQ5])]})])],"derivedFrom":makeQuery(id+"F3.boolean.opBoolean","COPY",FACE,{"derivedFrom":makeQuery(id+"F3.opExtrude","CAP_FACE",FACE,{"disambiguationData":[OSD([subQ5,subQ1,subQ6,subQ7,subQ4,subQ3,subQ2,subQ0])],"isStart":false})})}),makeQuery(id+"F8.opExtrude","SWEPT_FACE",FACE,{"disambiguationData":[OSD([sQuery(id+"F7.wireOp",EDGE,"E67")])]})]});}
            var Q5;
            Q5=makeQuery(id+"F8.boolean.opBoolean","INTERSECT",EDGE,{"disambiguationData":[OD(0.0)],"derivedFrom":[makeQuery(id+"F5.opExtrude","SWEPT_FACE",FACE,{"disambiguationData":[OSD([sQuery(id+"F4.wireOp",EDGE,"E30")])]}),makeQuery(id+"F8.opExtrude","SWEPT_FACE",FACE,{"disambiguationData":[OSD([sQuery(id+"F7.wireOp",EDGE,"E67")])]})]});
            fillet(context, id + "F14", {"entities" : qUnion([Q0, Q1, Q2, Q3, Q4, Q5]), "radius" : 3 * mm, "tangentPropagation" : true, "allowEdgeOverflow" : false});
        }
        {
            var Q0;
            Q0=makeQuery(id+"F1.opExtrude","CAP_EDGE",EDGE,{"disambiguationData":[OSD([sQuery(id+"F0.wireOp",EDGE,"E1.bottom")])],"isStart":false});
            fillet(context, id + "F15", {"entities" : qUnion([Q0]), "radius" : 2 * mm, "tangentPropagation" : true, "allowEdgeOverflow" : false});
        }
        {
            var Q0;
            {var subQ0=sQuery(id+"F0.wireOp",EDGE,"E21.filletArc");var subQ1=sQuery(id+"F0.wireOp",EDGE,"E7");var subQ2=sQuery(id+"F0.wireOp",EDGE,"E6");var subQ3=sQuery(id+"F0.wireOp",EDGE,"E5");var subQ4=sQuery(id+"F0.wireOp",EDGE,"E4");var subQ5=sQuery(id+"F0.wireOp",EDGE,"E22.filletArc");var subQ6=sQuery(id+"F0.wireOp",EDGE,"E1.bottom");var subQ7=sQuery(id+"F0.wireOp",EDGE,"E1.right");var subQ8=sQuery(id+"F0.wireOp",EDGE,"E1.top");var subQ9=sQuery(id+"F0.wireOp",EDGE,"E1.left");var subQ10=sQuery(id+"F0.wireOp",EDGE,"E23.filletArc");var subQ11=sQuery(id+"F0.wireOp",EDGE,"E24.filletArc");Q0=makeQuery(id+"F2.boolean.opBoolean","SPLIT",FACE,{"disambiguationData":[TD([makeQuery(id+"F1.opExtrude","SWEPT_FACE",FACE,{"disambiguationData":[OSD([subQ6])]})])],"derivedFrom":makeQuery(id+"F1.opExtrude","CAP_FACE",FACE,{"disambiguationData":[OSD([subQ6,subQ8,subQ9,subQ7,subQ4,subQ3,subQ2,subQ1,subQ0,subQ5,subQ10,subQ11])],"isStart":true})});}
            var sketch = newSketch(context, id + "F16", { "sketchPlane" : qUnion([Q0])});
            skLineSegment(sketch, "E79", {"start": v(-33, 135) * mm, "end": v(-15, 153) * mm});
            skLineSegment(sketch, "E80", {"start": v(33, 135) * mm, "end": v(15, 153) * mm});
            skLineSegment(sketch, "E81", {"start": v(-15, 153) * mm, "end": v(-15, 165) * mm});
            skLineSegment(sketch, "E82", {"start": v(15, 153) * mm, "end": v(15, 165) * mm});
            skArc(sketch, "E83", {"start": v(-15, 165) * mm, "mid": v(0, 180) * mm, "end": v(15, 165) * mm});
            skLineSegment(sketch, "E84", {"start": v(0, 165) * mm, "end": v(0, 135) * mm, "construction": true});
            skCircle(sketch, "E85", {"center": v(0, 165) * mm, "radius": 6 * mm});
            skLineSegment(sketch, "E86.MirrorCS", {"start": v(15, -153) * mm, "end": v(15, -165) * mm});
            skLineSegment(sketch, "E87.MirrorCS", {"start": v(-15, -153) * mm, "end": v(-15, -165) * mm});
            skLineSegment(sketch, "E88.MirrorCS", {"start": v(-33, -135) * mm, "end": v(-15, -153) * mm});
            skLineSegment(sketch, "E89.MirrorCS", {"start": v(0, -165) * mm, "end": v(0, -135) * mm, "construction": true});
            skArc(sketch, "E90.MirrorCS", {"start": v(-15, -165) * mm, "mid": v(0, -180) * mm, "end": v(15, -165) * mm});
            skCircle(sketch, "E91.MirrorC", {"center": v(0, -165) * mm, "radius": 6 * mm});
            skLineSegment(sketch, "E92.MirrorCS", {"start": v(33, -135) * mm, "end": v(15, -153) * mm});
            skSolve(sketch);
        }
        {
            var Q0;
            Q0=makeQuery(id+"F16.imprint","IMPRINT",FACE,{"disambiguationData":[TD([[makeQuery(id+"F16.imprint","IMPRINT",EDGE,{"derivedFrom":sQuery(id+"F16.wireOp",EDGE,"E86.MirrorCS")}),-1.0]])]});
            var Q1;
            Q1=makeQuery(id+"F0.imprint","IMPRINT",FACE,{"disambiguationData":[TD([[makeQuery(id+"F0.imprint","IMPRINT",EDGE,{"derivedFrom":sQuery(id+"F0.wireOp",EDGE,"E1.bottom")}),1.0]])]});
            var Q2;
            {var subQ0=sQuery(id+"F16.wireOp",EDGE,"E79");Q2=makeQuery(id+"F16.imprint","IMPRINT",FACE,{"disambiguationData":[TD([[makeQuery(id+"F16.imprint","IMPRINT",EDGE,{"derivedFrom":subQ0}),-1.0]])]});}
            var Q3;
            Q3=makeQuery(id+"F2.opExtrude","CAP_FACE",FACE,{"disambiguationData":[OSD([sQuery(id+"F0.wireOp",EDGE,"E12"),sQuery(id+"F0.wireOp",EDGE,"E13"),sQuery(id+"F0.wireOp",EDGE,"E14"),sQuery(id+"F0.wireOp",EDGE,"E15"),sQuery(id+"F0.wireOp",EDGE,"E17.filletArc"),sQuery(id+"F0.wireOp",EDGE,"E18.filletArc"),sQuery(id+"F0.wireOp",EDGE,"E19.filletArc"),sQuery(id+"F0.wireOp",EDGE,"E20.filletArc"),sQuery(id+"F0.wireOp",EDGE,"E25.0"),sQuery(id+"F0.wireOp",EDGE,"E25.1"),sQuery(id+"F0.wireOp",EDGE,"E25.2"),sQuery(id+"F0.wireOp",EDGE,"E25.3"),sQuery(id+"F0.wireOp",EDGE,"E25.4"),sQuery(id+"F0.wireOp",EDGE,"E25.5"),sQuery(id+"F0.wireOp",EDGE,"E25.6"),sQuery(id+"F0.wireOp",EDGE,"E25.7")])],"isStart":false});
            extrude(context, id + "F17", {"entities" : qUnion([Q0, Q1, Q2]), "operationType" : NewBodyOperationType.ADD, "endBound" : BoundingType.UP_TO_SURFACE, "endBoundEntityFace" : qUnion([Q3]), "depth" : 25 * mm});
        }
    });
